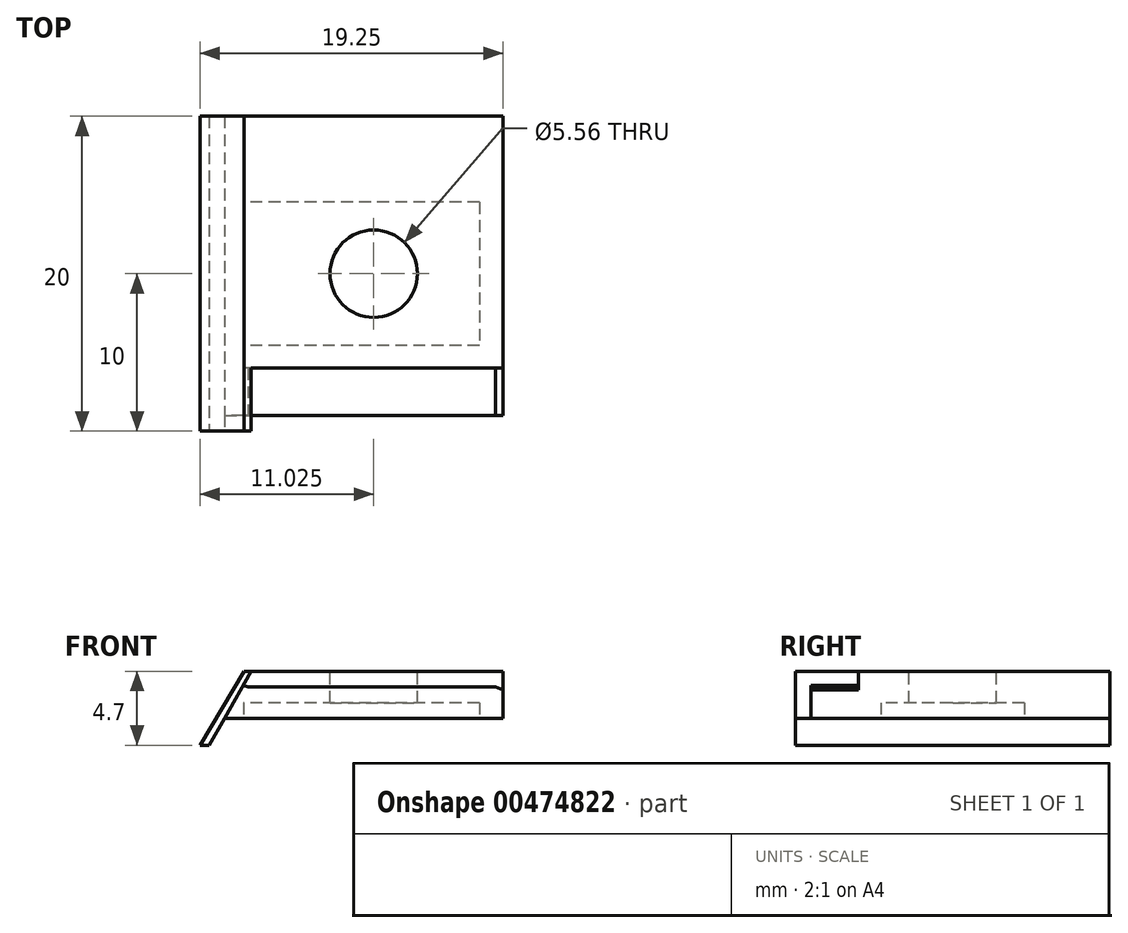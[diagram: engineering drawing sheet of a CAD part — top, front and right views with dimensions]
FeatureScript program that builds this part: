
annotation { "Feature Type Name" : "Feature", "Feature Type Description" : "" }
export const myFeature = defineFeature(function(context is Context, id is Id, definition is map)
    precondition{}
    {
        {
            var Q0;
            Q0=qCreatedBy(makeId("Front.planeOp"),FACE);
            var sketch = newSketch(context, id + "F0", { "sketchPlane" : qUnion([Q0])});
            skLineSegment(sketch, "E0", {"start": v(-19.25, -1.7) * mm, "end": v(-16.45, 3) * mm});
            skLineSegment(sketch, "E1", {"start": v(-16.45, 3) * mm, "end": v(0, 3) * mm});
            skLineSegment(sketch, "E2", {"start": v(0, 3) * mm, "end": v(0, 0) * mm});
            skLineSegment(sketch, "E3", {"start": v(0, 0) * mm, "end": v(-17.08, 0) * mm});
            skLineSegment(sketch, "E4", {"start": v(-17.08, 0) * mm, "end": v(-18.09, -1.7) * mm});
            skLineSegment(sketch, "E5", {"start": v(-18.09, -1.7) * mm, "end": v(-19.25, -1.7) * mm});
            skSolve(sketch);
        }
        {
            var Q0;
            Q0=makeQuery(id+"F0.imprint","IMPRINT",FACE,{"disambiguationData":[TD([[makeQuery(id+"F0.imprint","IMPRINT",EDGE,{"derivedFrom":sQuery(id+"F0.wireOp",EDGE,"E0")}),-1.0]])]});
            extrude(context, id + "F1", {"entities" : qUnion([Q0]), "depth" : 20 * mm});
        }
        {
            var Q0;
            Q0=makeQuery(id+"F1.opExtrude","CAP_FACE",FACE,{"disambiguationData":[OSD([sQuery(id+"F0.wireOp",EDGE,"E0"),sQuery(id+"F0.wireOp",EDGE,"E1"),sQuery(id+"F0.wireOp",EDGE,"E2"),sQuery(id+"F0.wireOp",EDGE,"E3"),sQuery(id+"F0.wireOp",EDGE,"E4"),sQuery(id+"F0.wireOp",EDGE,"E5")])],"isStart":false});
            var sketch = newSketch(context, id + "F2", { "sketchPlane" : qUnion([Q0])});
            skLineSegment(sketch, "E6", {"start": v(-0.5, 2) * mm, "end": v(0, 1.82) * mm});
            skLineSegment(sketch, "E7", {"start": v(0, 1.82) * mm, "end": v(0, 3) * mm});
            skLineSegment(sketch, "E8", {"start": v(0, 3) * mm, "end": v(-16, 3) * mm});
            skLineSegment(sketch, "E9", {"start": v(-0.5, 2) * mm, "end": v(-16.2, 2) * mm});
            skLineSegment(sketch, "E10", {"start": v(-16.2, 2) * mm, "end": v(-16.5, 2.1) * mm});
            skLineSegment(sketch, "E11", {"start": v(-16, 3) * mm, "end": v(-16.5, 2.1) * mm});
            skSolve(sketch);
        }
        {
            var Q0;
            Q0=qSketchRegion(id+"F2",true);
            extrude(context, id + "F3", {"entities" : qUnion([Q0]), "operationType" : NewBodyOperationType.REMOVE, "oppositeDirection" : true, "depth" : 4 * mm});
        }
        {
            var Q0;
            Q0=makeQuery(id+"F1.opExtrude","CAP_FACE",FACE,{"disambiguationData":[OSD([sQuery(id+"F0.wireOp",EDGE,"E0"),sQuery(id+"F0.wireOp",EDGE,"E1"),sQuery(id+"F0.wireOp",EDGE,"E2"),sQuery(id+"F0.wireOp",EDGE,"E3"),sQuery(id+"F0.wireOp",EDGE,"E4"),sQuery(id+"F0.wireOp",EDGE,"E5")])],"isStart":false});
            var sketch = newSketch(context, id + "F4", { "sketchPlane" : qUnion([Q0])});
            skLineSegment(sketch, "E12", {"start": v(0, 1.82) * mm, "end": v(-0.5, 2) * mm});
            skLineSegment(sketch, "E13", {"start": v(-0.5, 2) * mm, "end": v(-16.2, 2) * mm});
            skLineSegment(sketch, "E14", {"start": v(-16.2, 2) * mm, "end": v(-16.5, 2.1) * mm});
            skLineSegment(sketch, "E15", {"start": v(-16.5, 2.1) * mm, "end": v(-17.68, 0) * mm});
            skLineSegment(sketch, "E16", {"start": v(-17.68, 0) * mm, "end": v(0, 0) * mm});
            skLineSegment(sketch, "E17", {"start": v(0, 0) * mm, "end": v(0, 1.82) * mm});
            skSolve(sketch);
        }
        {
            var Q0;
            Q0=qSketchRegion(id+"F4",true);
            extrude(context, id + "F5", {"entities" : qUnion([Q0]), "operationType" : NewBodyOperationType.REMOVE, "oppositeDirection" : true, "depth" : 1 * mm});
        }
        {
            var Q0;
            Q0=makeQuery(id+"F1.opExtrude","CAP_FACE",FACE,{"disambiguationData":[OSD([sQuery(id+"F0.wireOp",EDGE,"E0"),sQuery(id+"F0.wireOp",EDGE,"E1"),sQuery(id+"F0.wireOp",EDGE,"E2"),sQuery(id+"F0.wireOp",EDGE,"E3"),sQuery(id+"F0.wireOp",EDGE,"E4"),sQuery(id+"F0.wireOp",EDGE,"E5")])],"isStart":false});
            var sketch = newSketch(context, id + "F6", { "sketchPlane" : qUnion([Q0])});
            skLineSegment(sketch, "E18", {"start": v(-18.09, -1.7) * mm, "end": v(-17.08, 0) * mm});
            skLineSegment(sketch, "E19", {"start": v(-17.08, 0) * mm, "end": v(-17.68, 0) * mm});
            skLineSegment(sketch, "E20", {"start": v(-17.68, 0) * mm, "end": v(-18.67, -1.7) * mm});
            skLineSegment(sketch, "E21", {"start": v(-18.67, -1.7) * mm, "end": v(-18.09, -1.7) * mm});
            skSolve(sketch);
        }
        {
            var Q0;
            Q0=qSketchRegion(id+"F6",true);
            extrude(context, id + "F7", {"entities" : qUnion([Q0]), "operationType" : NewBodyOperationType.REMOVE, "endBound" : BoundingType.THROUGH_ALL, "oppositeDirection" : true, "depth" : 25 * mm});
        }
        {
            var Q0;
            Q0=makeQuery(id+"F1.opExtrude","SWEPT_FACE",FACE,{"disambiguationData":[OSD([sQuery(id+"F0.wireOp",EDGE,"E1")])]});
            var sketch = newSketch(context, id + "F8", { "sketchPlane" : qUnion([Q0])});
            skLineSegment(sketch, "E22", {"start": v(-16.45, -20) * mm, "end": v(-16.45, 0) * mm, "construction": true});
            skPoint(sketch, "E23", {"position": v(-16.45, -10) * mm});
            skLineSegment(sketch, "E24", {"start": v(-16.45, -10) * mm, "end": v(0, -10) * mm, "construction": true});
            skPoint(sketch, "E25", {"position": v(-8.22, -10) * mm});
            skSolve(sketch);
        }
        {
            var Q0;
            Q0=sQuery(id+"F8.wireOp",EDGE,"E24");
            cPlane(context, id + "F9", {"entities" : qUnion([Q0]), "cplaneType" : CPlaneType.LINE_ANGLE, "offset" : 25 * mm, "angle" : 0 * degree, "width" : 150 * mm, "height" : 150 * mm});
        }
        {
            var Q0;
            Q0=makeQuery(id+"F7.boolean.opBoolean","MERGE",FACE,{"derivedFrom":[makeQuery(id+"F1.opExtrude","SWEPT_FACE",FACE,{"disambiguationData":[OSD([sQuery(id+"F0.wireOp",EDGE,"E3")])]}),makeQuery(id+"F7.opExtrude","SWEPT_FACE",FACE,{"disambiguationData":[OSD([sQuery(id+"F6.wireOp",EDGE,"E19")])]})]});
            var sketch = newSketch(context, id + "F10", { "sketchPlane" : qUnion([Q0])});
            skLineSegment(sketch, "E26.bottom", {"start": v(-1.5, 5.45) * mm, "end": v(-16.5, 5.45) * mm});
            skLineSegment(sketch, "E26.top", {"start": v(-1.5, 14.55) * mm, "end": v(-16.5, 14.55) * mm});
            skLineSegment(sketch, "E26.left", {"start": v(-1.5, 5.45) * mm, "end": v(-1.5, 14.55) * mm});
            skLineSegment(sketch, "E26.right", {"start": v(-16.5, 5.45) * mm, "end": v(-16.5, 14.55) * mm});
            skSolve(sketch);
        }
        {
            var Q0;
            Q0=qSketchRegion(id+"F10",true);
            extrude(context, id + "F11", {"entities" : qUnion([Q0]), "operationType" : NewBodyOperationType.REMOVE, "oppositeDirection" : true, "depth" : 1 * mm});
        }
        {
            var Q0;
            Q0=sQuery(id+"F8.wireOp",VERTEX,"E25");
            var Q1;
            Q1=makeQuery(id+"F1.opExtrude","SWEPT_BODY",BODY,{"disambiguationData":[OSD([sQuery(id+"F0.wireOp",EDGE,"E0"),sQuery(id+"F0.wireOp",EDGE,"E1"),sQuery(id+"F0.wireOp",EDGE,"E2"),sQuery(id+"F0.wireOp",EDGE,"E3"),sQuery(id+"F0.wireOp",EDGE,"E4"),sQuery(id+"F0.wireOp",EDGE,"E5")])]});
            hole(context, id + "F12", {"style" : HoleStyle.SIMPLE, "endStyle" : HoleEndStyle.THROUGH, "standardTappedOrClearance" : lookupTablePath({ "standard" : "ANSI", "engagement" : "75%", "pitch" : "32 tpi", "size" : "1/4", "type" : "Tapped" }), "standardBlindInLast" : lookupTablePath({ "standard" : "ANSI", "engagement" : "75%", "pitch" : "32 tpi", "size" : "1/4", "type" : "Tapped" }), "holeDiameter" : 5.56 * mm, "showTappedDepth" : true, "isTappedThrough" : true, "tappedDepth" : 12 * mm, "tapClearance" : 3, "locations" : qUnion([Q0]), "scope" : qUnion([Q1]), "majorDiameter" : 6.35 * mm});
        }
    });
